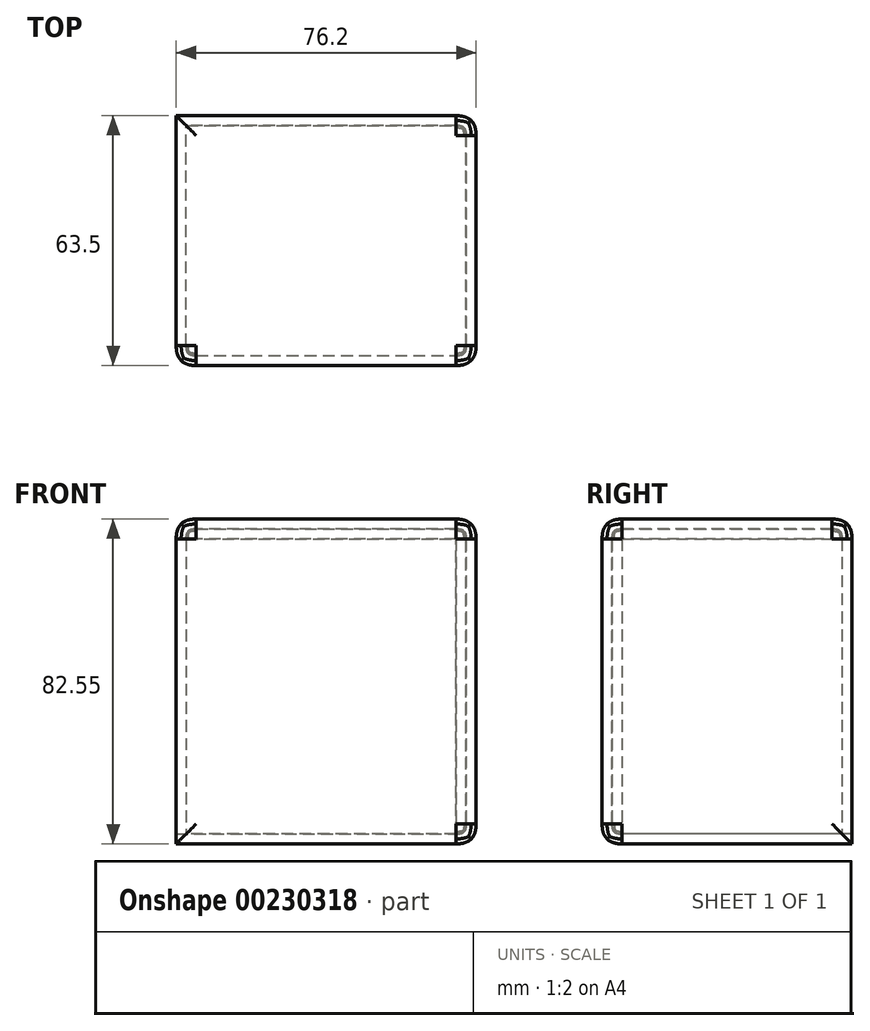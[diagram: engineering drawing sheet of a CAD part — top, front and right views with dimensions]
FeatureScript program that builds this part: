
annotation { "Feature Type Name" : "Feature", "Feature Type Description" : "" }
export const myFeature = defineFeature(function(context is Context, id is Id, definition is map)
    precondition{}
    {
        {
            var Q0;
            Q0=qCreatedBy(makeId("Top.planeOp"),FACE);
            var sketch = newSketch(context, id + "F0", { "sketchPlane" : qUnion([Q0])});
            skLineSegment(sketch, "E0.bottom", {"start": v(-32.82, 25.29) * mm, "end": v(43.38, 25.29) * mm});
            skLineSegment(sketch, "E0.top", {"start": v(-32.82, -38.21) * mm, "end": v(43.38, -38.21) * mm});
            skLineSegment(sketch, "E0.left", {"start": v(-32.82, 25.29) * mm, "end": v(-32.82, -38.21) * mm});
            skLineSegment(sketch, "E0.right", {"start": v(43.38, 25.29) * mm, "end": v(43.38, -38.21) * mm});
            skSolve(sketch);
        }
        {
            var Q0;
            Q0=makeQuery(id+"F0.imprint","IMPRINT",FACE,{"disambiguationData":[TD([[makeQuery(id+"F0.imprint","IMPRINT",EDGE,{"derivedFrom":sQuery(id+"F0.wireOp",EDGE,"E0.bottom")}),-1.0]])]});
            extrude(context, id + "F1", {"entities" : qUnion([Q0]), "depth" : 82.55 * mm});
        }
        {
            var Q0;
            Q0=makeQuery(id+"F1.opExtrude","CAP_EDGE",EDGE,{"disambiguationData":[OSD([sQuery(id+"F0.wireOp",EDGE,"E0.top")])],"isStart":false});
            var Q1;
            Q1=makeQuery(id+"F1.opExtrude","CAP_EDGE",EDGE,{"disambiguationData":[OSD([sQuery(id+"F0.wireOp",EDGE,"E0.right")])],"isStart":false});
            var Q2;
            Q2=makeQuery(id+"F1.opExtrude","SWEPT_EDGE",EDGE,{"disambiguationData":[OSD([sQuery(id+"F0.wireOp",EDGE,"E0.top"),sQuery(id+"F0.wireOp",EDGE,"E0.right")])]});
            var Q3;
            Q3=makeQuery(id+"F1.opExtrude","CAP_EDGE",EDGE,{"disambiguationData":[OSD([sQuery(id+"F0.wireOp",EDGE,"E0.top")])],"isStart":true});
            var Q4;
            Q4=makeQuery(id+"F1.opExtrude","SWEPT_EDGE",EDGE,{"disambiguationData":[OSD([sQuery(id+"F0.wireOp",EDGE,"E0.top"),sQuery(id+"F0.wireOp",EDGE,"E0.left")])]});
            var Q5;
            Q5=makeQuery(id+"F1.opExtrude","SWEPT_EDGE",EDGE,{"disambiguationData":[OSD([sQuery(id+"F0.wireOp",EDGE,"E0.bottom"),sQuery(id+"F0.wireOp",EDGE,"E0.right")])]});
            var Q6;
            Q6=makeQuery(id+"F1.opExtrude","CAP_EDGE",EDGE,{"disambiguationData":[OSD([sQuery(id+"F0.wireOp",EDGE,"E0.right")])],"isStart":true});
            var Q7;
            Q7=makeQuery(id+"F1.opExtrude","CAP_FACE",FACE,{"disambiguationData":[OSD([sQuery(id+"F0.wireOp",EDGE,"E0.bottom"),sQuery(id+"F0.wireOp",EDGE,"E0.top"),sQuery(id+"F0.wireOp",EDGE,"E0.left"),sQuery(id+"F0.wireOp",EDGE,"E0.right")])],"isStart":false});
            fillet(context, id + "F2", {"entities" : qUnion([Q0, Q1, Q2, Q3, Q4, Q5, Q6, Q7]), "radius" : 5.08 * mm, "tangentPropagation" : true, "rho" : 0.5, "crossSection" : FilletCrossSection.CONIC, "allowEdgeOverflow" : false});
        }
        {
            var Q0;
            Q0=makeQuery(id+"F1.opExtrude","SWEPT_FACE",FACE,{"disambiguationData":[OSD([sQuery(id+"F0.wireOp",EDGE,"E0.left")])]});
            var Q1;
            Q1=makeQuery(id+"F1.opExtrude","SWEPT_FACE",FACE,{"disambiguationData":[OSD([sQuery(id+"F0.wireOp",EDGE,"E0.bottom")])]});
            shell(context, id + "F3", {"entities" : qUnion([Q0, Q1]), "thickness" : 2.54 * mm});
        }
    });
